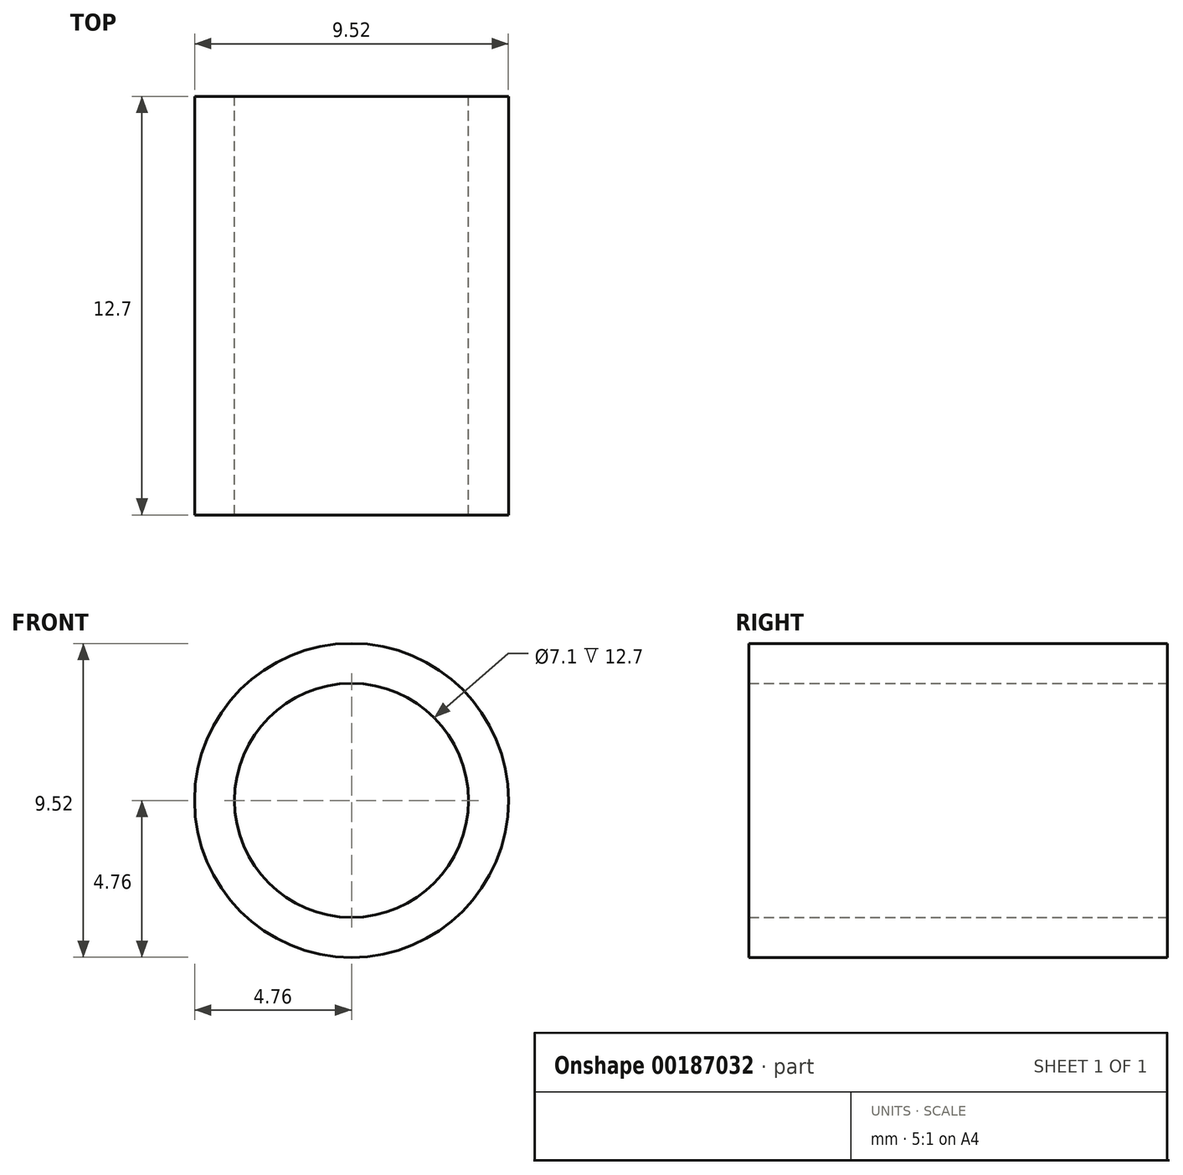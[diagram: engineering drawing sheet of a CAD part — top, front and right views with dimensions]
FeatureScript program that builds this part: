
annotation { "Feature Type Name" : "Feature", "Feature Type Description" : "" }
export const myFeature = defineFeature(function(context is Context, id is Id, definition is map)
    precondition{}
    {
        {
            var Q0;
            Q0=qCreatedBy(makeId("Front.planeOp"),FACE);
            var sketch = newSketch(context, id + "F0", { "sketchPlane" : qUnion([Q0])});
            skCircle(sketch, "E0", {"center": v(0, 0) * mm, "radius": 4.76 * mm});
            skCircle(sketch, "E1", {"center": v(0, 0) * mm, "radius": 3.55 * mm});
            skSolve(sketch);
        }
        {
            var Q0;
            Q0=makeQuery(id+"F0.imprint","IMPRINT",FACE,{"disambiguationData":[TD([[makeQuery(id+"F0.imprint","IMPRINT",EDGE,{"derivedFrom":sQuery(id+"F0.wireOp",EDGE,"E0")}),1.0]])]});
            extrude(context, id + "F1", {"entities" : qUnion([Q0]), "depth" : 12.7 * mm});
        }
    });
